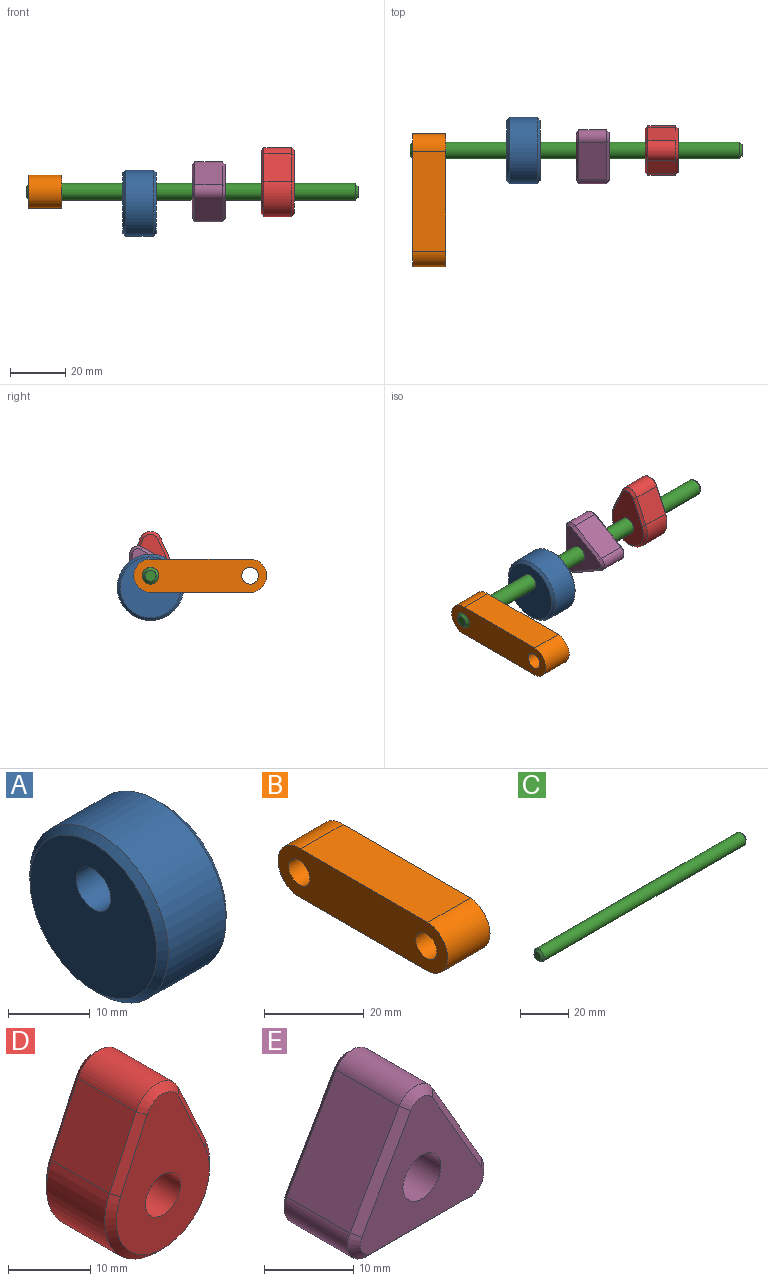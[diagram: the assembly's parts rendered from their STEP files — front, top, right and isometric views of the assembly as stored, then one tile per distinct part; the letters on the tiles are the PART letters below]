
ASSEMBLY  parts=5 mates=4
PART A: 6 faces, bbox 12x24x24 mm
  f0: cylinder r=3mm len=12mm, axis (-1,0,0), area 226.2mm2, adj f2,f3
  f1: cylinder r=12mm len=24mm, axis (-1,0,0), area 754mm2, adj f4,f5
  f2: plane 22x22mm, normal (1,0,0), area 351.9mm2, adj f0,f5
  f3: plane 22x22mm, normal (-1,0,0), area 351.9mm2, adj f0,f4
  f4: cone r=12mm half-angle=45deg, axis (1,0,0), area 102.2mm2, adj f1,f3
  f5: cone r=11mm half-angle=45deg, axis (-1,0,0), area 102.2mm2, adj f1,f2
PART B: 8 faces, bbox 12x48x12 mm
  f0: plane 36x12mm, normal (0,0,1), area 432mm2, adj f1,f5,f6,f7
  f1: cylinder r=6mm len=12mm, axis (-1,0,0), area 224.3mm2, adj f0,f2,f6,f7
  f2: plane 35.47x12mm, normal (0,0,-1), area 425.6mm2, adj f1,f5,f6,f7
  f3: cylinder r=3mm len=12mm, axis (-1,0,0), area 226.2mm2, adj f6,f7
  f4: cylinder r=3mm len=12mm, axis (-1,0,0), area 226.2mm2, adj f6,f7
  f5: cylinder r=6mm len=12mm, axis (-1,0,0), area 234.5mm2, adj f0,f2,f6,f7
  f6: plane 48x12mm, normal (1,0,0), area 487.8mm2, adj f0,f1,f2,f3,f4,f5
  f7: plane 48x12mm, normal (-1,0,0), area 487.8mm2, adj f0,f1,f2,f3,f4,f5
PART C: 5 faces, bbox 120x6x6 mm
  f0: cylinder r=3mm len=118mm, axis (-1,0,0), area 2224.2mm2, adj f3,f4
  f1: plane 4x4mm, normal (1,0,0), area 12.6mm2, adj f4
  f2: plane 4x4mm, normal (-1,0,0), area 12.6mm2, adj f3
  f3: cone r=3mm half-angle=45deg, axis (1,0,0), area 22.2mm2, adj f0,f2
  f4: cone r=2mm half-angle=45deg, axis (-1,0,0), area 22.2mm2, adj f0,f1
PART D: 15 faces, bbox 18x12x25 mm
  f0: plane 10x9.92mm, normal (-0.91,0,0.42), area 109.1mm2, adj f1,f4,f7,f12
  f1: cylinder r=9mm len=18mm, axis (0,1,0), area 360.1mm2, adj f0,f2,f9,f14
  f2: plane 10x9.92mm, normal (0.91,0,0.42), area 109.1mm2, adj f1,f4,f10,f13
  f3: cylinder r=3mm len=12mm, axis (0,1,0), area 226.2mm2, adj f5,f6
  f4: cylinder r=4mm len=10mm, axis (0,1,0), area 91.3mm2, adj f0,f2,f8,f11
  f5: plane 23x16mm, normal (0,-1,0), area 230mm2, adj f3,f11,f12,f13,f14
  f6: plane 23x16mm, normal (0,1,0), area 230mm2, adj f3,f7,f8,f9,f10
  f7: plane 10.33x5.45mm, normal (-0.64,0.71,0.29), area 15.4mm2, adj f0,f6,f8,f9
  f8: cone r=4mm half-angle=45deg, axis (0,-1,0), area 11.3mm2, adj f4,f6,f7,f10
  f9: cone r=9mm half-angle=45deg, axis (0,-1,0), area 48.1mm2, adj f1,f6,f7,f10
  f10: plane 10.33x5.45mm, normal (0.64,0.71,0.29), area 15.4mm2, adj f2,f6,f8,f9
  f11: cone r=3mm half-angle=45deg, axis (0,1,0), area 11.3mm2, adj f4,f5,f12,f13
  f12: plane 10.33x5.45mm, normal (-0.64,-0.71,0.29), area 15.4mm2, adj f0,f5,f11,f14
  f13: plane 10.33x5.45mm, normal (0.64,-0.71,0.29), area 15.4mm2, adj f2,f5,f11,f14
  f14: cone r=8mm half-angle=45deg, axis (0,1,0), area 48.1mm2, adj f1,f5,f12,f13
PART E: 21 faces, bbox 21.6x12x19.5 mm
  f0: cylinder r=3mm len=10mm, axis (0,1,0), area 62.8mm2, adj f1,f6,f12,f18
  f1: plane 13.5x10mm, normal (0.87,0,0.5), area 155.9mm2, adj f0,f2,f10,f16
  f2: cylinder r=3mm len=10mm, axis (0,1,0), area 62.8mm2, adj f1,f3,f9,f15
  f3: plane 13.5x10mm, normal (-0.87,0,0.5), area 155.9mm2, adj f2,f4,f11,f17
  f4: cylinder r=3mm len=10mm, axis (0,1,0), area 62.8mm2, adj f3,f6,f13,f19
  f5: cylinder r=3mm len=12mm, axis (0,1,0), area 226.2mm2, adj f7,f8
  f6: plane 15.59x10mm, normal (0,0,-1), area 155.9mm2, adj f0,f4,f14,f20
  f7: plane 19.59x17.5mm, normal (0,-1,0), area 183mm2, adj f5,f15,f16,f17,f18,f19,f20
  f8: plane 19.59x17.5mm, normal (0,1,0), area 183mm2, adj f5,f9,f10,f11,f12,f13,f14
  f9: cone r=3mm half-angle=45deg, axis (0,-1,0), area 7.4mm2, adj f2,f8,f10,f11
  f10: plane 14x8.66mm, normal (0.61,0.71,0.35), area 22mm2, adj f1,f8,f9,f12
  f11: plane 14x8.66mm, normal (-0.61,0.71,0.35), area 22mm2, adj f3,f8,f9,f13
  f12: cone r=3mm half-angle=45deg, axis (0,-1,0), area 7.4mm2, adj f0,f8,f10,f14
  f13: cone r=3mm half-angle=45deg, axis (0,-1,0), area 7.4mm2, adj f4,f8,f11,f14
  f14: plane 15.59x1mm, normal (0,0.71,-0.71), area 22mm2, adj f6,f8,f12,f13
  f15: cone r=2mm half-angle=45deg, axis (0,1,0), area 7.4mm2, adj f2,f7,f16,f17
  f16: plane 14x8.66mm, normal (0.61,-0.71,0.35), area 22mm2, adj f1,f7,f15,f18
  f17: plane 14x8.66mm, normal (-0.61,-0.71,0.35), area 22mm2, adj f3,f7,f15,f19
  f18: cone r=2mm half-angle=45deg, axis (0,1,0), area 7.4mm2, adj f0,f7,f16,f20
  f19: cone r=2mm half-angle=45deg, axis (0,1,0), area 7.4mm2, adj f4,f7,f17,f20
  f20: plane 15.59x1mm, normal (0,-0.71,-0.71), area 22mm2, adj f6,f7,f18,f19
PLACE A t=(-6.17,-80.62,12.22)mm
PLACE B t=(-40.17,-106.53,-29.33)mm
PLACE C t=(18.83,-37.32,-28.31)mm
PLACE D rot(axis=(0,0,1),90deg) t=(43.83,86.78,46.28)mm
PLACE E rot(axis=(0.58,-0.58,0.58),120deg) t=(18.83,41.73,62.7)mm
MATE fastened D.f1 <-> C.f0  axis (-1,0,0) through (49.83,41.73,46.28)mm
MATE fastened B.f4 <-> C.f0  axis (-1,0,0) through (-40.17,41.73,46.28)mm
MATE fastened E.f5 <-> C.f0  axis (-1,0,0) through (24.83,41.73,46.28)mm
MATE fastened A.f0 <-> C.f0  axis (-1,0,0) through (-0.17,41.73,46.28)mm
